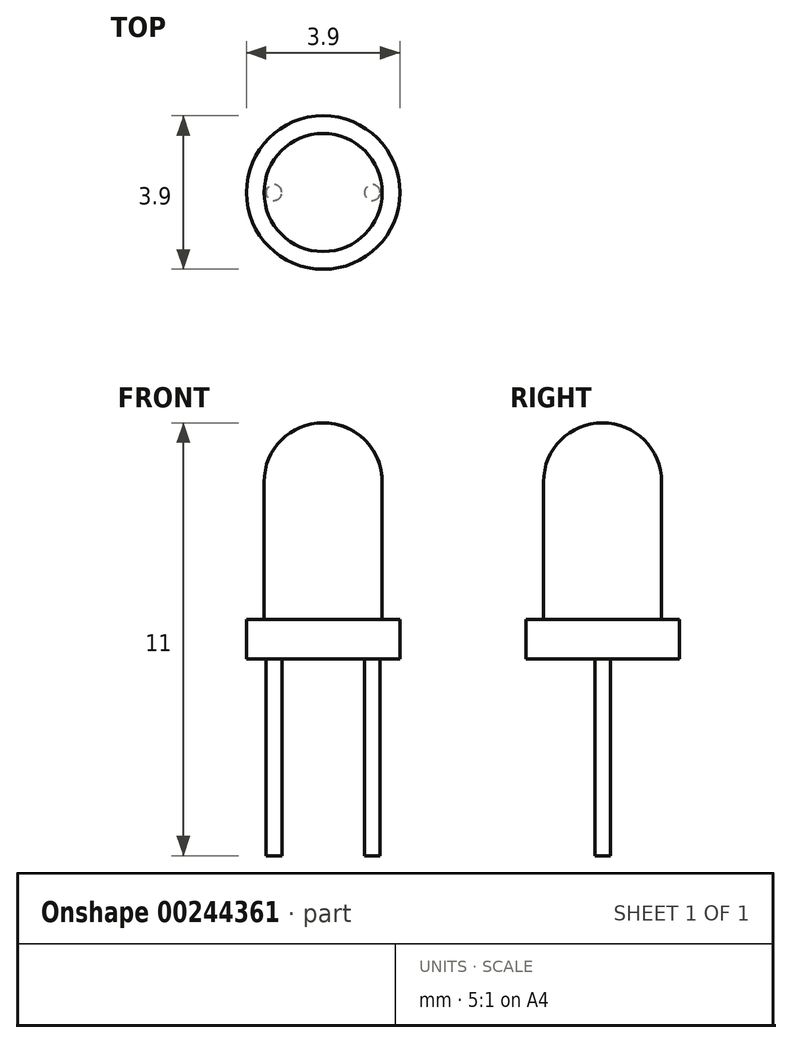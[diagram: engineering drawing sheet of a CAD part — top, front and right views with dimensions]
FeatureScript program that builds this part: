
annotation { "Feature Type Name" : "Feature", "Feature Type Description" : "" }
export const myFeature = defineFeature(function(context is Context, id is Id, definition is map)
    precondition{}
    {
        {
            var Q0;
            Q0=qCreatedBy(makeId("Top.planeOp"),FACE);
            var sketch = newSketch(context, id + "F0", { "sketchPlane" : qUnion([Q0])});
            skCircle(sketch, "E0", {"center": v(0, 0) * mm, "radius": 1.5 * mm});
            skSolve(sketch);
        }
        {
            var Q0;
            Q0 = qSketchRegion(id + "F0", true);
            extrude(context, id + "F1", {"entities" : qUnion([Q0]), "depth" : 5 * mm});
        }
        {
            var Q0;
            Q0=makeQuery(id+"F1.opExtrude","CAP_FACE",FACE,{"disambiguationData":[OSD([sQuery(id+"F0.wireOp",EDGE,"E0")])],"isStart":true});
            var sketch = newSketch(context, id + "F2", { "sketchPlane" : qUnion([Q0])});
            skCircle(sketch, "E1", {"center": v(0, 0) * mm, "radius": 1.95 * mm});
            skSolve(sketch);
        }
        {
            var Q0;
            Q0 = qSketchRegion(id + "F2", true);
            extrude(context, id + "F3", {"entities" : qUnion([Q0]), "operationType" : NewBodyOperationType.ADD, "depth" : 1 * mm});
        }
        {
            var Q0;
            Q0=makeQuery(id+"F3.opExtrude","CAP_FACE",FACE,{"disambiguationData":[OSD([sQuery(id+"F2.wireOp",EDGE,"E1")])],"isStart":false});
            var sketch = newSketch(context, id + "F4", { "sketchPlane" : qUnion([Q0])});
            skCircle(sketch, "E2", {"center": v(-1.25, 0) * mm, "radius": 0.2 * mm});
            skCircle(sketch, "E3.MirrorC", {"center": v(1.25, 0) * mm, "radius": 0.2 * mm});
            skSolve(sketch);
        }
        {
            var Q0;
            Q0 = qSketchRegion(id + "F4", true);
            extrude(context, id + "F5", {"entities" : qUnion([Q0]), "depth" : 5 * mm});
        }
        {
            var Q0;
            Q0=makeQuery(id+"F1.opExtrude","CAP_EDGE",EDGE,{"disambiguationData":[OSD([sQuery(id+"F0.wireOp",EDGE,"E0")])],"isStart":false});
            fillet(context, id + "F6", {"entities" : qUnion([Q0]), "radius" : 1.5 * mm, "tangentPropagation" : true, "allowEdgeOverflow" : false});
        }
    });
